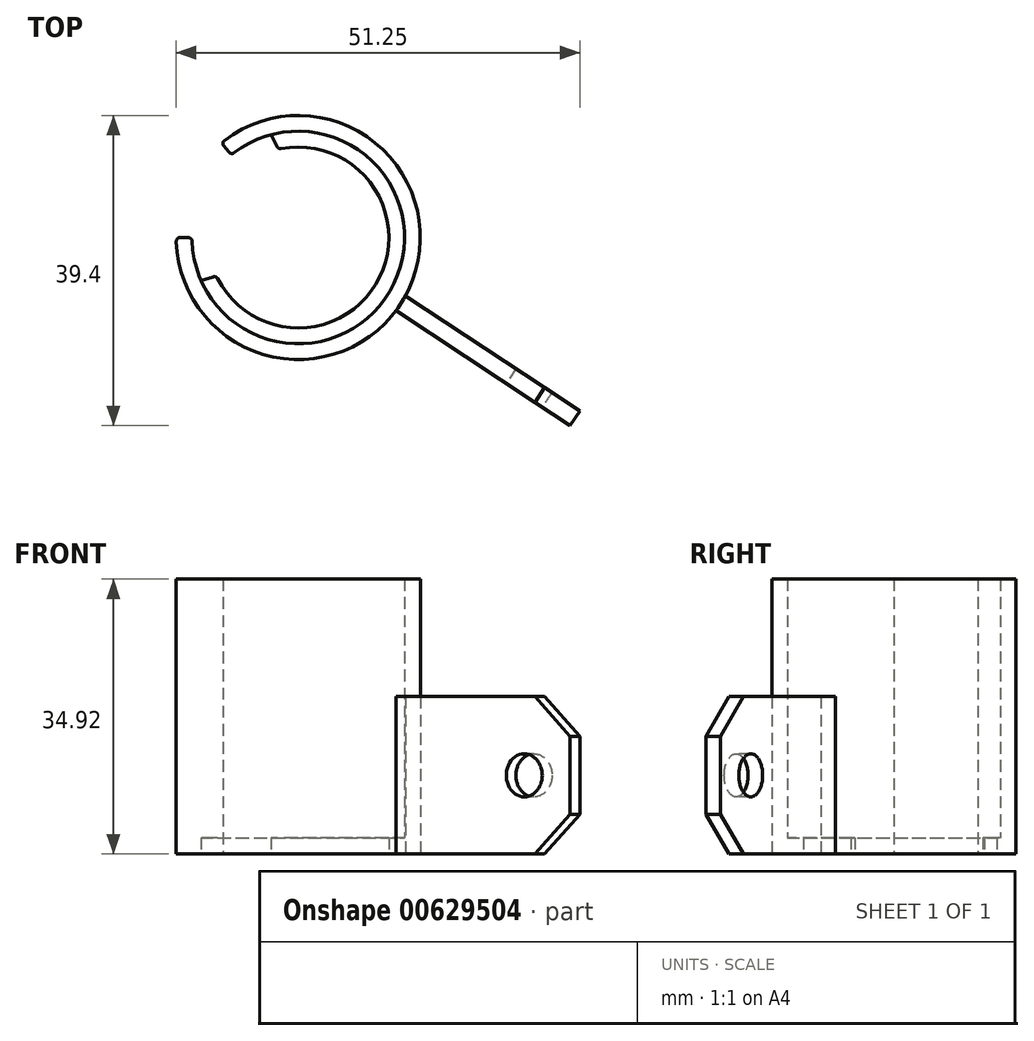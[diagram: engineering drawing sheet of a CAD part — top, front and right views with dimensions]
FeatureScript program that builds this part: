
annotation { "Feature Type Name" : "Feature", "Feature Type Description" : "" }
export const myFeature = defineFeature(function(context is Context, id is Id, definition is map)
    precondition{}
    {
        {
            var Q0;
            Q0=qCreatedBy(makeId("Top.planeOp"),FACE);
            var sketch = newSketch(context, id + "F0", { "sketchPlane" : qUnion([Q0])});
            skArc(sketch, "E0", {"start": v(-13.5, -0.47) * mm, "mid": v(12.19, -5.8) * mm, "end": v(-8.14, 10.77) * mm});
            skArc(sketch, "E1.0", {"start": v(-15.5, -0.5) * mm, "mid": v(14, -6.66) * mm, "end": v(-9.38, 12.34) * mm});
            skLineSegment(sketch, "E2", {"start": v(-15, 0) * mm, "end": v(-13.98, 0) * mm});
            skPoint(sketch, "E3.visualSharp", {"position": v(-13.5, 0) * mm});
            skArc(sketch, "E3.filletArc", {"start": v(-13.5, -0.47) * mm, "mid": v(-13.64, -0.14) * mm, "end": v(-13.98, 0) * mm});
            skPoint(sketch, "E4.visualSharp", {"position": v(-15.5, 0) * mm});
            skArc(sketch, "E4.filletArc", {"start": v(-15, 0) * mm, "mid": v(-15.35, -0.15) * mm, "end": v(-15.5, -0.5) * mm});
            skLineSegment(sketch, "E5", {"start": v(-9.46, 11.65) * mm, "end": v(-8.81, 10.85) * mm});
            skPoint(sketch, "E6.visualSharp", {"position": v(-9.77, 12.03) * mm});
            skArc(sketch, "E6.filletArc", {"start": v(-9.38, 12.34) * mm, "mid": v(-9.57, 12.01) * mm, "end": v(-9.46, 11.65) * mm});
            skPoint(sketch, "E7.visualSharp", {"position": v(-8.51, 10.48) * mm});
            skArc(sketch, "E7.filletArc", {"start": v(-8.81, 10.85) * mm, "mid": v(-8.5, 10.67) * mm, "end": v(-8.14, 10.77) * mm});
            skArc(sketch, "E8.0", {"start": v(-10.24, -5.24) * mm, "mid": v(10.34, -5.04) * mm, "end": v(-2.17, 11.3) * mm});
            skLineSegment(sketch, "E9", {"start": v(-3.43, 13.06) * mm, "end": v(-2.7, 11.56) * mm});
            skPoint(sketch, "E10", {"position": v(-10.82, -3.9) * mm});
            skPoint(sketch, "E11", {"position": v(-10.54, -4.6) * mm});
            skLineSegment(sketch, "E12", {"start": v(-10.81, -5) * mm, "end": v(-12.35, -5.46) * mm});
            skPoint(sketch, "E13.orphan", {"position": v(-11.5, -0.4) * mm});
            skPoint(sketch, "E14.orphan", {"position": v(-6.93, 9.17) * mm});
            skPoint(sketch, "E15.visualSharp", {"position": v(-2.53, 11.22) * mm});
            skArc(sketch, "E15.filletArc", {"start": v(-2.7, 11.56) * mm, "mid": v(-2.48, 11.34) * mm, "end": v(-2.17, 11.3) * mm});
            skPoint(sketch, "E16.visualSharp", {"position": v(-10.41, -4.88) * mm});
            skArc(sketch, "E16.filletArc", {"start": v(-10.24, -5.24) * mm, "mid": v(-10.48, -5.02) * mm, "end": v(-10.81, -5) * mm});
            skLineSegment(sketch, "E17", {"start": v(12.42, -9.28) * mm, "end": v(34.53, -23.9) * mm});
            skLineSegment(sketch, "E18", {"start": v(35.21, -23.76) * mm, "end": v(35.22, -23.74) * mm});
            skPoint(sketch, "E19.visualSharp", {"position": v(34.94, -24.17) * mm});
            skPoint(sketch, "E20.visualSharp", {"position": v(35.5, -23.33) * mm});
            skLineSegment(sketch, "E21.0", {"start": v(13.65, -7.41) * mm, "end": v(35.76, -22.03) * mm});
            skLineSegment(sketch, "E22", {"start": v(13.65, -7.41) * mm, "end": v(13.62, -7.4) * mm});
            skLineSegment(sketch, "E23", {"start": v(34.53, -23.9) * mm, "end": v(35.76, -22.03) * mm});
            skSolve(sketch);
        }
        {
            var Q0;
            Q0=makeQuery(id+"F0.imprint","IMPRINT",FACE,{"disambiguationData":[TD([[makeQuery(id+"F0.imprint","IMPRINT",EDGE,{"derivedFrom":sQuery(id+"F0.wireOp",EDGE,"E0")}),-1.0]])]});
            extrude(context, id + "F1", {"entities" : qUnion([Q0]), "depth" : 34.92 * mm});
        }
        {
            var Q0;
            Q0=makeQuery(id+"F0.imprint","IMPRINT",FACE,{"disambiguationData":[TD([[makeQuery(id+"F0.imprint","IMPRINT",EDGE,{"derivedFrom":sQuery(id+"F0.wireOp",EDGE,"E8.0")}),-1.0]])]});
            extrude(context, id + "F2", {"entities" : qUnion([Q0]), "operationType" : NewBodyOperationType.ADD, "depth" : 2.06 * mm});
        }
        {
            var Q0;
            {var subQ0=sQuery(id+"F0.wireOp",EDGE,"E17");Q0=makeQuery(id+"F0.imprint","IMPRINT",FACE,{"disambiguationData":[TD([[makeQuery(id+"F0.imprint","IMPRINT",EDGE,{"derivedFrom":subQ0}),1.0]])]});}
            extrude(context, id + "F3", {"entities" : qUnion([Q0]), "operationType" : NewBodyOperationType.ADD, "depth" : 19.99 * mm});
        }
        {
            var Q0;
            Q0=makeQuery(id+"F3.opExtrude","SWEPT_FACE",FACE,{"disambiguationData":[OSD([sQuery(id+"F0.wireOp",EDGE,"E17")])]});
            var sketch = newSketch(context, id + "F4", { "sketchPlane" : qUnion([Q0])});
            skLineSegment(sketch, "E24", {"start": v(36.63, 19.99) * mm, "end": v(41.99, 14.93) * mm});
            skPoint(sketch, "E25", {"position": v(41.99, 19.99) * mm});
            skPoint(sketch, "E26", {"position": v(41.99, 5.05) * mm});
            skLineSegment(sketch, "E27", {"start": v(36.63, 0) * mm, "end": v(41.99, 5.05) * mm});
            skLineSegment(sketch, "E28", {"start": v(36.63, 19.99) * mm, "end": v(41.99, 19.99) * mm});
            skLineSegment(sketch, "E29", {"start": v(36.63, 0) * mm, "end": v(41.99, 0) * mm});
            skLineSegment(sketch, "E30", {"start": v(41.99, 0) * mm, "end": v(41.99, 5.05) * mm});
            skSolve(sketch);
        }
        {
            var Q0;
            Q0=qSketchRegion(id+"F4",true);
            var Q1;
            {var subQ0=sQuery(id+"F4.wireOp",EDGE,"E24");Q1=makeQuery(id+"F4.imprint","IMPRINT",FACE,{"disambiguationData":[TD([[makeQuery(id+"F4.imprint","IMPRINT",EDGE,{"derivedFrom":subQ0}),1.0]])]});}
            extrude(context, id + "F5", {"entities" : qUnion([Q0, Q1]), "operationType" : NewBodyOperationType.REMOVE, "oppositeDirection" : true, "depth" : 25.4 * mm});
        }
        {
            var Q0;
            Q0=makeQuery(id+"F3.opExtrude","SWEPT_FACE",FACE,{"disambiguationData":[OSD([sQuery(id+"F0.wireOp",EDGE,"E17")])]});
            var sketch = newSketch(context, id + "F6", { "sketchPlane" : qUnion([Q0])});
            skPoint(sketch, "E31", {"position": v(15.47, 10) * mm});
            skPoint(sketch, "E32", {"position": v(35, 10) * mm});
            skPoint(sketch, "E33.orphan", {"position": v(15.47, 19.99) * mm});
            skCircle(sketch, "E34", {"center": v(35, 10) * mm, "radius": 2.74 * mm});
            skSolve(sketch);
        }
        {
            var Q0;
            Q0=makeQuery(id+"F6.imprint","IMPRINT",FACE,{"disambiguationData":[TD([[makeQuery(id+"F6.imprint","IMPRINT",EDGE,{"derivedFrom":sQuery(id+"F6.wireOp",EDGE,"E34")}),1.0]])]});
            extrude(context, id + "F7", {"entities" : qUnion([Q0]), "operationType" : NewBodyOperationType.REMOVE, "oppositeDirection" : true, "depth" : 6.35 * mm});
        }
    });
